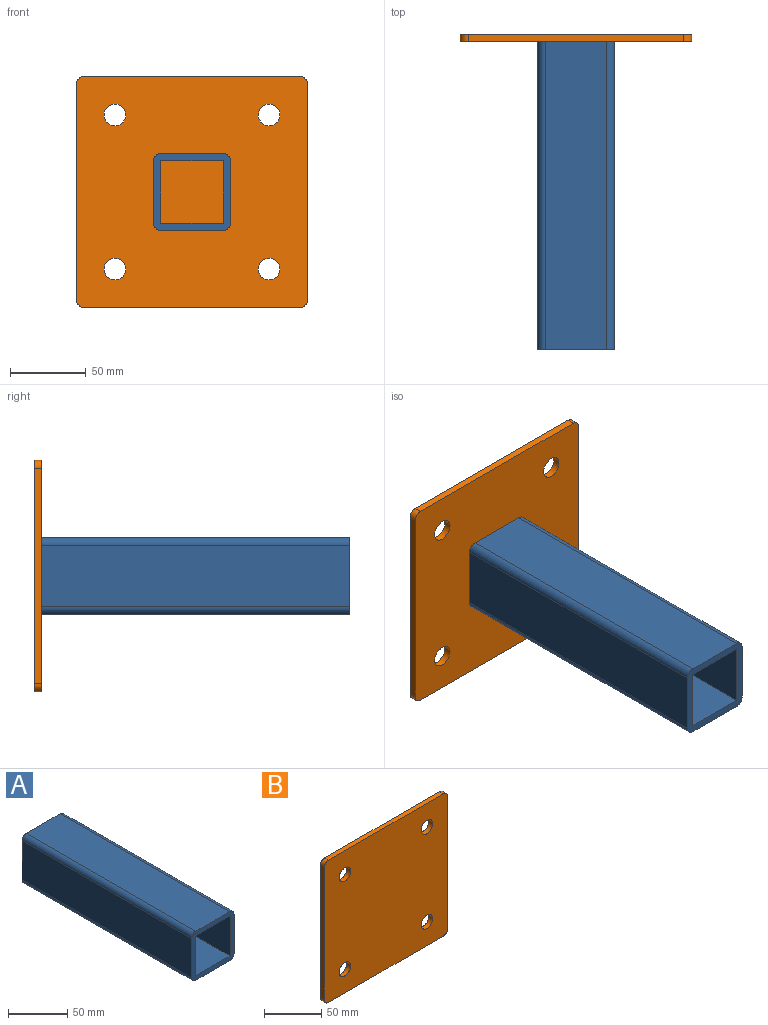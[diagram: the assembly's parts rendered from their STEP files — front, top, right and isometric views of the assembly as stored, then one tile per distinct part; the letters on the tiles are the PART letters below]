
ASSEMBLY  parts=2 mates=1
PART A: 14 faces, bbox 50.8x203.2x50.8 mm
  f0: plane 203.2x40.64mm, normal (0,0,1), area 8258mm2, adj f8,f9,f10,f13
  f1: plane 203.2x40.64mm, normal (-1,0,0), area 8258mm2, adj f8,f9,f10,f11
  f2: plane 203.2x40.64mm, normal (0,0,-1), area 8258mm2, adj f8,f9,f11,f12
  f3: plane 203.2x41.28mm, normal (1,0,0), area 8387.1mm2, adj f4,f6,f8,f9
  f4: plane 203.2x41.28mm, normal (0,0,-1), area 8387.1mm2, adj f3,f5,f8,f9
  f5: plane 203.2x41.28mm, normal (-1,0,0), area 8387.1mm2, adj f4,f6,f8,f9
  f6: plane 203.2x41.28mm, normal (0,0,1), area 8387.1mm2, adj f3,f5,f8,f9
  f7: plane 203.2x40.64mm, normal (1,0,0), area 8258mm2, adj f8,f9,f12,f13
  f8: plane 50.8x50.8mm, normal (0,-1,0), area 854.9mm2, adj f0,f1,f2,f3,f4,f5,f6,f7
  f9: plane 50.8x50.8mm, normal (0,1,0), area 854.9mm2, adj f0,f1,f2,f3,f4,f5,f6,f7
  f10: cylinder r=5.08mm len=203.2mm, axis (0,-1,0), area 1621.5mm2, adj f0,f1,f8,f9
  f11: cylinder r=5.08mm len=203.2mm, axis (0,1,0), area 1621.5mm2, adj f1,f2,f8,f9
  f12: cylinder r=5.08mm len=203.2mm, axis (0,-1,0), area 1621.5mm2, adj f2,f7,f8,f9
  f13: cylinder r=5.08mm len=203.2mm, axis (0,1,0), area 1621.5mm2, adj f0,f7,f8,f9
PART B: 14 faces, bbox 152.4x4.8x152.4 mm
  f0: plane 142.24x4.76mm, normal (0,0,1), area 677.4mm2, adj f4,f5,f6,f9
  f1: plane 142.24x4.76mm, normal (-1,0,0), area 677.4mm2, adj f4,f5,f6,f7
  f2: plane 142.24x4.76mm, normal (0,0,-1), area 677.4mm2, adj f4,f5,f7,f8
  f3: plane 142.24x4.76mm, normal (1,0,0), area 677.4mm2, adj f4,f5,f8,f9
  f4: plane 152.4x152.4mm, normal (0,-1,0), area 22562.3mm2, adj f0,f1,f2,f3,f6,f7,f8,f9
  f5: plane 152.4x152.4mm, normal (0,1,0), area 22562.3mm2, adj f0,f1,f2,f3,f6,f7,f8,f9
  f6: cylinder r=5.08mm len=5.08mm, axis (0,-1,0), area 38mm2, adj f0,f1,f4,f5
  f7: cylinder r=5.08mm len=5.08mm, axis (0,1,0), area 38mm2, adj f1,f2,f4,f5
  f8: cylinder r=5.08mm len=5.08mm, axis (0,-1,0), area 38mm2, adj f2,f3,f4,f5
  f9: cylinder r=5.08mm len=5.08mm, axis (0,1,0), area 38mm2, adj f0,f3,f4,f5
  f10: cylinder r=7.14mm len=14.29mm, axis (0,-1,0), area 213.8mm2, adj f4,f5
  f11: cylinder r=7.14mm len=14.29mm, axis (0,-1,0), area 213.8mm2, adj f4,f5
  f12: cylinder r=7.14mm len=14.29mm, axis (0,-1,0), area 213.8mm2, adj f4,f5
  f13: cylinder r=7.14mm len=14.29mm, axis (0,-1,0), area 213.8mm2, adj f4,f5
PLACE A t=(-24.58,-13.38,14.55)mm
PLACE B t=(-32.41,-8.62,7.45)mm
MATE fastened A.f9 <-> B.f4  axis (0,1,0) through (-30.21,-13.38,9.66)mm
